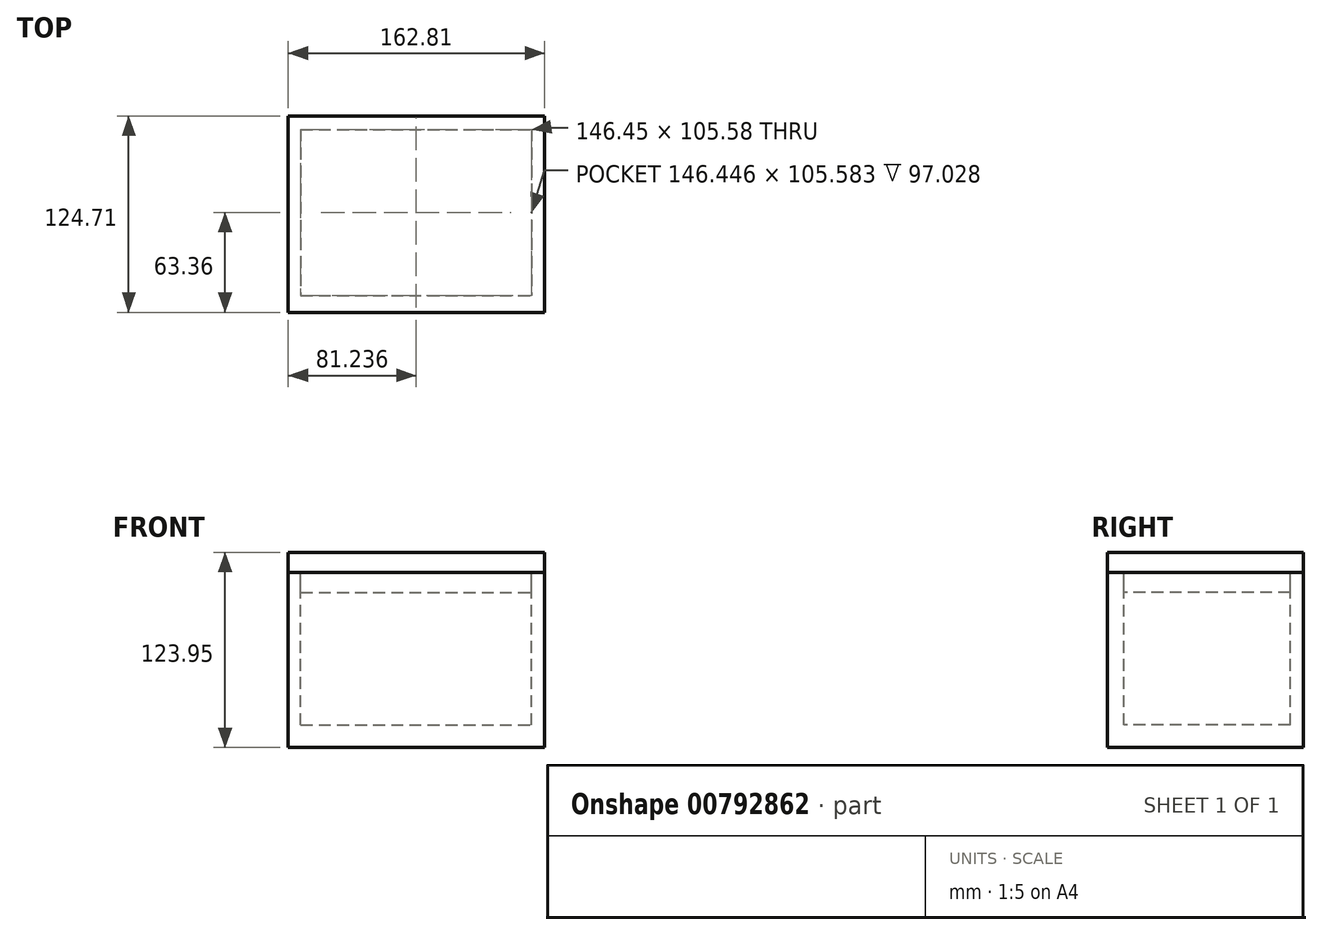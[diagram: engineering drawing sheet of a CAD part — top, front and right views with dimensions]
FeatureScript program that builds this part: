
annotation { "Feature Type Name" : "Feature", "Feature Type Description" : "" }
export const myFeature = defineFeature(function(context is Context, id is Id, definition is map)
    precondition{}
    {
        {
            var Q0;
            Q0=qCreatedBy(makeId("Right.planeOp"),FACE);
            var sketch = newSketch(context, id + "F0", { "sketchPlane" : qUnion([Q0])});
            skLineSegment(sketch, "E0.bottom", {"start": v(-56.26, 56.26) * mm, "end": v(68.45, 56.26) * mm});
            skLineSegment(sketch, "E0.top", {"start": v(-56.26, -55) * mm, "end": v(68.45, -55) * mm});
            skLineSegment(sketch, "E0.left", {"start": v(-56.26, 56.26) * mm, "end": v(-56.26, -55) * mm});
            skLineSegment(sketch, "E0.right", {"start": v(68.45, 56.26) * mm, "end": v(68.45, -55) * mm});
            skSolve(sketch);
        }
        {
            var Q0;
            Q0 = qSketchRegion(id + "F0", true);
            extrude(context, id + "F1", {"entities" : qUnion([Q0]), "depth" : 162.8 * mm, "offsetDistance" : 25.4 * mm});
        }
        {
            var Q0;
            Q0=makeQuery(id+"F1.opExtrude","SWEPT_FACE",FACE,{"disambiguationData":[OSD([sQuery(id+"F0.wireOp",EDGE,"E0.bottom")])]});
            var sketch = newSketch(context, id + "F2", { "sketchPlane" : qUnion([Q0])});
            skLineSegment(sketch, "E1.bottom", {"start": v(8.01, 59.9) * mm, "end": v(154.46, 59.9) * mm});
            skLineSegment(sketch, "E1.top", {"start": v(8.01, -45.7) * mm, "end": v(154.46, -45.7) * mm});
            skLineSegment(sketch, "E1.left", {"start": v(8.01, 59.9) * mm, "end": v(8.01, -45.7) * mm});
            skLineSegment(sketch, "E1.right", {"start": v(154.46, 59.9) * mm, "end": v(154.46, -45.7) * mm});
            skSolve(sketch);
        }
        {
            var Q0;
            Q0 = qSketchRegion(id + "F2", true);
            extrude(context, id + "F3", {"entities" : qUnion([Q0]), "operationType" : NewBodyOperationType.REMOVE, "oppositeDirection" : true, "depth" : 97.03 * mm, "offsetDistance" : 25.4 * mm});
        }
        {
            var Q0;
            Q0=makeQuery(id+"F1.opExtrude","SWEPT_FACE",FACE,{"disambiguationData":[OSD([sQuery(id+"F0.wireOp",EDGE,"E0.right")])]});
            var sketch = newSketch(context, id + "F4", { "sketchPlane" : qUnion([Q0])});
            skSolve(sketch);
        }
        {
            var Q0;
            Q0=makeQuery(id+"F1.opExtrude","SWEPT_FACE",FACE,{"disambiguationData":[OSD([sQuery(id+"F0.wireOp",EDGE,"E0.bottom")])]});
            var sketch = newSketch(context, id + "F5", { "sketchPlane" : qUnion([Q0])});
            skLineSegment(sketch, "E2.bottom", {"start": v(162.81, -56.26) * mm, "end": v(0, -56.26) * mm});
            skLineSegment(sketch, "E2.top", {"start": v(162.81, 68.45) * mm, "end": v(0, 68.45) * mm});
            skLineSegment(sketch, "E2.left", {"start": v(162.81, -56.26) * mm, "end": v(162.81, 68.45) * mm});
            skLineSegment(sketch, "E2.right", {"start": v(0, -56.26) * mm, "end": v(0, 68.45) * mm});
            skSolve(sketch);
        }
        {
            var Q0;
            Q0 = qSketchRegion(id + "F5", true);
            extrude(context, id + "F6", {"entities" : qUnion([Q0]), "endBound" : BoundingType.SYMMETRIC, "depth" : 25.4 * mm, "offsetDistance" : 25.4 * mm});
        }
        {
            var Q0;
            Q0=makeQuery(id+"F1.opExtrude","SWEPT_BODY",BODY,{"disambiguationData":[OSD([sQuery(id+"F0.wireOp",EDGE,"E0.bottom"),sQuery(id+"F0.wireOp",EDGE,"E0.top"),sQuery(id+"F0.wireOp",EDGE,"E0.left"),sQuery(id+"F0.wireOp",EDGE,"E0.right")])]});
            var Q1;
            Q1=makeQuery(id+"F6.opExtrude","SWEPT_BODY",BODY,{"disambiguationData":[OSD([sQuery(id+"F5.wireOp",EDGE,"E2.bottom"),sQuery(id+"F5.wireOp",EDGE,"E2.top"),sQuery(id+"F5.wireOp",EDGE,"E2.left"),sQuery(id+"F5.wireOp",EDGE,"E2.right")])]});
            booleanBodies(context, id + "F7", {"operationType" : BooleanOperationType.SUBTRACTION, "tools" : qUnion([Q0]), "targets" : qUnion([Q1]), "keepTools" : true});
        }
    });
